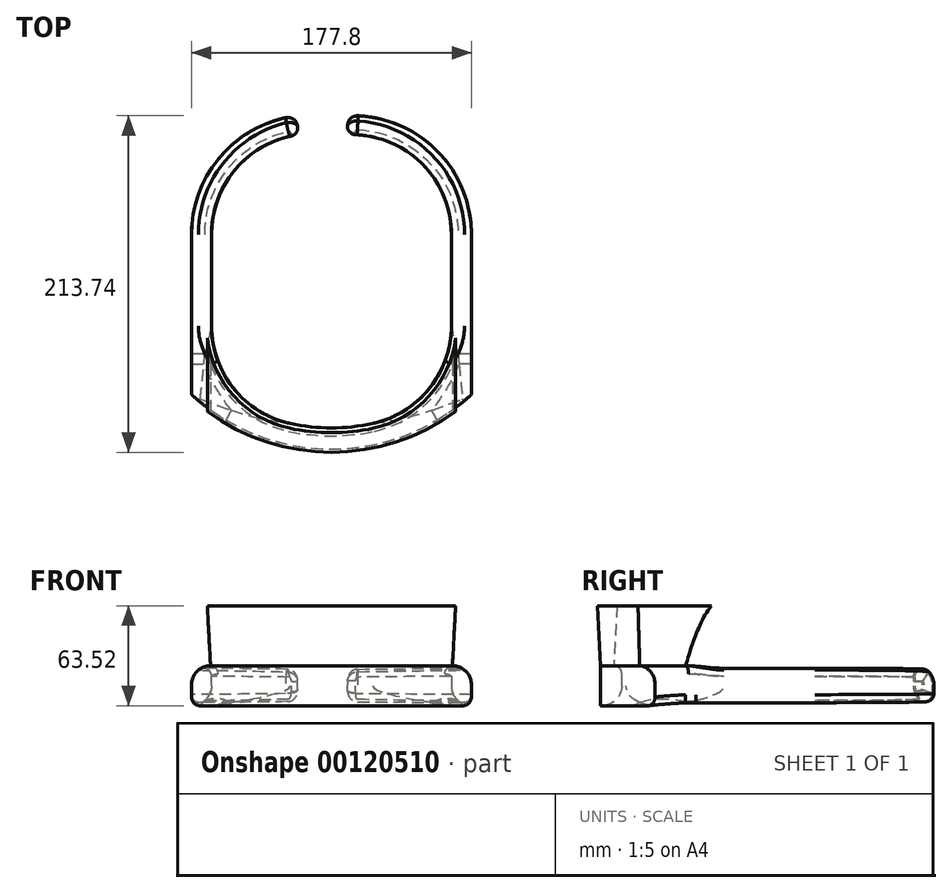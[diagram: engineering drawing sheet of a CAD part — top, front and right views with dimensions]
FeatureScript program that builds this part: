
annotation { "Feature Type Name" : "Feature", "Feature Type Description" : "" }
export const myFeature = defineFeature(function(context is Context, id is Id, definition is map)
    precondition{}
    {
        {
            var Q0;
            Q0=qCreatedBy(makeId("Top.planeOp"),FACE);
            var sketch = newSketch(context, id + "F0", { "sketchPlane" : qUnion([Q0])});
            skLineSegment(sketch, "E0", {"start": v(-46.12, 53.95) * mm, "end": v(-46.12, -42.57) * mm});
            skLineSegment(sketch, "E1", {"start": v(106.28, -42.57) * mm, "end": v(106.28, 53.95) * mm});
            skArc(sketch, "E2", {"start": v(-46.12, -42.57) * mm, "mid": v(30.08, -68.86) * mm, "end": v(106.28, -42.57) * mm});
            skLineSegment(sketch, "E3", {"start": v(-46.12, 53.95) * mm, "end": v(-58.82, 53.95) * mm});
            skLineSegment(sketch, "E4", {"start": v(-58.82, 53.95) * mm, "end": v(-58.82, -47.65) * mm});
            skLineSegment(sketch, "E5", {"start": v(106.28, 53.95) * mm, "end": v(118.98, 53.95) * mm});
            skLineSegment(sketch, "E6", {"start": v(118.98, 53.95) * mm, "end": v(118.98, -47.65) * mm});
            skArc(sketch, "E7", {"start": v(-58.82, -47.65) * mm, "mid": v(30.08, -82.35) * mm, "end": v(118.98, -47.65) * mm});
            skSolve(sketch);
        }
        {
            var Q0;
            Q0 = qSketchRegion(id + "F0", true);
            extrude(context, id + "F1", {"entities" : qUnion([Q0]), "oppositeDirection" : true, "depth" : 25.4 * mm});
        }
        {
            var Q0;
            Q0=makeQuery(id+"F1.opExtrude","CAP_FACE",FACE,{"disambiguationData":[OSD([sQuery(id+"F0.wireOp",EDGE,"E0"),sQuery(id+"F0.wireOp",EDGE,"E1"),sQuery(id+"F0.wireOp",EDGE,"E2"),sQuery(id+"F0.wireOp",EDGE,"E3"),sQuery(id+"F0.wireOp",EDGE,"E4"),sQuery(id+"F0.wireOp",EDGE,"E5"),sQuery(id+"F0.wireOp",EDGE,"E6"),sQuery(id+"F0.wireOp",EDGE,"E7")])],"isStart":true});
            var sketch = newSketch(context, id + "F2", { "sketchPlane" : qUnion([Q0])});
            skArc(sketch, "E8", {"start": v(8.76, 117.38) * mm, "mid": v(-30.5, 95.9) * mm, "end": v(-46.12, 53.95) * mm});
            skArc(sketch, "E9", {"start": v(8.48, 129.4) * mm, "mid": v(-39.55, 104.5) * mm, "end": v(-58.82, 53.95) * mm});
            skLineSegment(sketch, "E10", {"start": v(8.48, 129.4) * mm, "end": v(8.76, 117.38) * mm});
            skArc(sketch, "E11", {"start": v(106.28, 53.95) * mm, "mid": v(86.84, 99.67) * mm, "end": v(40.42, 117.38) * mm});
            skArc(sketch, "E12", {"start": v(118.98, 53.95) * mm, "mid": v(95.67, 108.51) * mm, "end": v(40.13, 129.4) * mm});
            skLineSegment(sketch, "E13", {"start": v(40.42, 117.38) * mm, "end": v(40.13, 129.4) * mm});
            skSolve(sketch);
        }
        {
            var Q0;
            Q0=makeQuery(id+"F2.imprint","IMPRINT",FACE,{"disambiguationData":[TD([[makeQuery(id+"F2.imprint","IMPRINT",EDGE,{"derivedFrom":sQuery(id+"F2.wireOp",EDGE,"E8")}),-1.0]])]});
            var Q1;
            Q1=makeQuery(id+"F2.imprint","IMPRINT",FACE,{"disambiguationData":[TD([[makeQuery(id+"F2.imprint","IMPRINT",EDGE,{"derivedFrom":sQuery(id+"F2.wireOp",EDGE,"E11")}),-1.0]])]});
            extrude(context, id + "F3", {"entities" : qUnion([Q0, Q1]), "operationType" : NewBodyOperationType.ADD, "oppositeDirection" : true, "depth" : 25.4 * mm});
        }
        {
            var Q0;
            Q0=makeQuery(id+"F3.opExtrude","CAP_EDGE",EDGE,{"disambiguationData":[OSD([sQuery(id+"F2.wireOp",EDGE,"E9")])],"isStart":true});
            var Q1;
            Q1=makeQuery(id+"F1.opExtrude","CAP_EDGE",EDGE,{"disambiguationData":[OSD([sQuery(id+"F0.wireOp",EDGE,"E6")])],"isStart":true});
            fillet(context, id + "F4", {"entities" : qUnion([Q0, Q1]), "radius" : 12.06 * mm, "tangentPropagation" : true, "allowEdgeOverflow" : false});
        }
        {
            var Q0;
            Q0=makeQuery(id+"F4.opFillet","BLEND_EDGE",EDGE,{"blendedFrom":[makeQuery(id+"F3.opExtrude","CAP_EDGE",EDGE,{"disambiguationData":[OSD([sQuery(id+"F2.wireOp",EDGE,"E12")])],"isStart":true}),makeQuery(id+"F3.opExtrude","SWEPT_FACE",FACE,{"disambiguationData":[OSD([sQuery(id+"F2.wireOp",EDGE,"E13")])]})],"blendedInto":[makeQuery(id+"F3.opExtrude","SWEPT_FACE",FACE,{"disambiguationData":[OSD([sQuery(id+"F2.wireOp",EDGE,"E13")])]})]});
            var Q1;
            Q1=makeQuery(id+"F4.opFillet","BLEND_EDGE",EDGE,{"blendedFrom":[makeQuery(id+"F3.opExtrude","CAP_EDGE",EDGE,{"disambiguationData":[OSD([sQuery(id+"F2.wireOp",EDGE,"E9")])],"isStart":true}),makeQuery(id+"F3.opExtrude","SWEPT_FACE",FACE,{"disambiguationData":[OSD([sQuery(id+"F2.wireOp",EDGE,"E10")])]})],"blendedInto":[makeQuery(id+"F3.opExtrude","SWEPT_FACE",FACE,{"disambiguationData":[OSD([sQuery(id+"F2.wireOp",EDGE,"E10")])]})]});
            fillet(context, id + "F5", {"entities" : qUnion([Q0, Q1]), "radius" : 6.35 * mm, "tangentPropagation" : true, "allowEdgeOverflow" : false});
        }
        {
            var Q0;
            Q0=makeQuery(id+"F3.opExtrude","CAP_EDGE",EDGE,{"disambiguationData":[OSD([sQuery(id+"F2.wireOp",EDGE,"E8")])],"isStart":false});
            var Q1;
            Q1=makeQuery(id+"F3.opExtrude","CAP_EDGE",EDGE,{"disambiguationData":[OSD([sQuery(id+"F2.wireOp",EDGE,"E11")])],"isStart":false});
            fillet(context, id + "F6", {"entities" : qUnion([Q0, Q1]), "radius" : 12.7 * mm, "tangentPropagation" : true, "allowEdgeOverflow" : false});
        }
        {
            var Q0;
            Q0=makeQuery(id+"F1.opExtrude","CAP_EDGE",EDGE,{"disambiguationData":[OSD([sQuery(id+"F0.wireOp",EDGE,"E2")])],"isStart":false});
            fillet(context, id + "F7", {"entities" : qUnion([Q0]), "radius" : 12.7 * mm, "tangentPropagation" : true, "allowEdgeOverflow" : false});
        }
        {
            var Q0;
            Q0=makeQuery(id+"F1.opExtrude","SWEPT_EDGE",EDGE,{"disambiguationData":[OSD([sQuery(id+"F0.wireOp",EDGE,"E1"),sQuery(id+"F0.wireOp",EDGE,"E2")])]});
            var Q1;
            Q1=makeQuery(id+"F1.opExtrude","SWEPT_EDGE",EDGE,{"disambiguationData":[OSD([sQuery(id+"F0.wireOp",EDGE,"E0"),sQuery(id+"F0.wireOp",EDGE,"E2")])]});
            fillet(context, id + "F8", {"entities" : qUnion([Q0, Q1]), "radius" : 63.5 * mm, "tangentPropagation" : true, "allowEdgeOverflow" : false});
        }
        {
            var Q0;
            Q0=makeQuery(id+"F6.opFillet","BLEND_EDGE",EDGE,{"blendedFrom":[makeQuery(id+"F3.opExtrude","CAP_EDGE",EDGE,{"disambiguationData":[OSD([sQuery(id+"F2.wireOp",EDGE,"E8")])],"isStart":false}),makeQuery(id+"F3.opExtrude","SWEPT_FACE",FACE,{"disambiguationData":[OSD([sQuery(id+"F2.wireOp",EDGE,"E9")])]})],"blendedInto":[makeQuery(id+"F3.opExtrude","SWEPT_FACE",FACE,{"disambiguationData":[OSD([sQuery(id+"F2.wireOp",EDGE,"E9")])]})]});
            var Q1;
            Q1=makeQuery(id+"F6.opFillet","BLEND_EDGE",EDGE,{"blendedFrom":[makeQuery(id+"F3.opExtrude","CAP_EDGE",EDGE,{"disambiguationData":[OSD([sQuery(id+"F2.wireOp",EDGE,"E11")])],"isStart":false}),makeQuery(id+"F3.opExtrude","SWEPT_FACE",FACE,{"disambiguationData":[OSD([sQuery(id+"F2.wireOp",EDGE,"E12")])]})],"blendedInto":[makeQuery(id+"F3.opExtrude","SWEPT_FACE",FACE,{"disambiguationData":[OSD([sQuery(id+"F2.wireOp",EDGE,"E12")])]})]});
            fillet(context, id + "F9", {"entities" : qUnion([Q0, Q1]), "radius" : 5.08 * mm, "tangentPropagation" : true, "allowEdgeOverflow" : false});
        }
        {
            var Q0;
            {var subQ0=sQuery(id+"F0.wireOp",EDGE,"E5");var subQ1=sQuery(id+"F0.wireOp",EDGE,"E3");Q0=makeQuery(id+"F3.boolean.opBoolean","MERGE",FACE,{"derivedFrom":[makeQuery(id+"F1.opExtrude","CAP_FACE",FACE,{"disambiguationData":[OSD([sQuery(id+"F0.wireOp",EDGE,"E0"),sQuery(id+"F0.wireOp",EDGE,"E1"),sQuery(id+"F0.wireOp",EDGE,"E2"),subQ1,sQuery(id+"F0.wireOp",EDGE,"E4"),subQ0,sQuery(id+"F0.wireOp",EDGE,"E6"),sQuery(id+"F0.wireOp",EDGE,"E7")])],"isStart":true}),makeQuery(id+"F3.opExtrude","CAP_FACE",FACE,{"disambiguationData":[OSD([subQ1,sQuery(id+"F2.wireOp",EDGE,"E8"),sQuery(id+"F2.wireOp",EDGE,"E9"),sQuery(id+"F2.wireOp",EDGE,"E10")])],"isStart":true}),makeQuery(id+"F3.opExtrude","CAP_FACE",FACE,{"disambiguationData":[OSD([subQ0,sQuery(id+"F2.wireOp",EDGE,"E11"),sQuery(id+"F2.wireOp",EDGE,"E12"),sQuery(id+"F2.wireOp",EDGE,"E13")])],"isStart":true})]});}
            extrude(context, id + "F10", {"entities" : qUnion([Q0]), "operationType" : NewBodyOperationType.ADD, "depth" : 38.1 * mm, "hasDraft" : true, "draftAngle" : 3 * degree});
        }
    });
